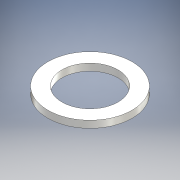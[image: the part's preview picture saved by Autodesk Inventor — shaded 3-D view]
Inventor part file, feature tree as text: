
AUTODESK INVENTOR PART (.ipt)
format: ipt  version: 2016 (Build 200138000, 138)  size: 97,792 bytes
history: native  units: mm
features: other x1, extrude x1, sketch x1
ambient origin geometry x8: Origin, YZ Plane, XZ Plane, XY Plane, X Axis, Y Axis, Z Axis, Center Point
bodies: Body1 (feature_tree)
feature tree (3):
  other  "ソリッド1"
  extrude  "押し出し1"  Depth=4.0mm
  sketch  "スケッチ1"
